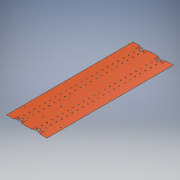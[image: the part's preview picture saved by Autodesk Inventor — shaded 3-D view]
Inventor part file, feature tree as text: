
AUTODESK INVENTOR PART (.ipt)
format: ipt  version: 2019 (Build 230136000, 136)  size: 379,904 bytes
history: native  units: mm
features: mirror x5, extrude x4, other x4
ambient origin geometry x8: Origin, YZ Plane, XZ Plane, XY Plane, X Axis, Y Axis, Z Axis, Center Point
bodies: Solid1 (feature_tree)
feature tree (13):
  extrude  "Skin Body"  Depth=1609.0mm
  extrude  "Feature Cut"  Depth=804.5mm
  mirror  "Feature Cut Side Mirror"
  mirror  "Feature Cut Mirror"
  extrude  "End Cut"  Depth=424.0mm
  mirror  "End Cut Mirror"
  extrude  "Slot Cut"  Depth=212.0mm
  mirror  "Slot Cut Side Mirror"
  mirror  "Slot Cut Mirror"
  other  "Skin Scheme"
  other  "Feature Cut Outline"
  other  "End Cut Outline"
  other  "Slot Cut Outline"
